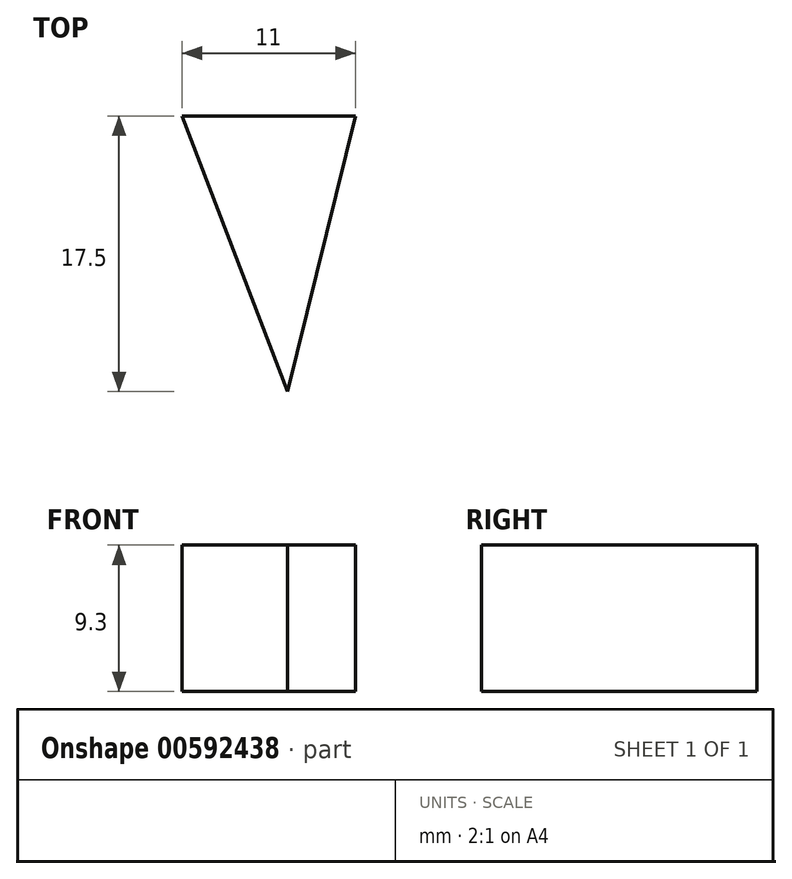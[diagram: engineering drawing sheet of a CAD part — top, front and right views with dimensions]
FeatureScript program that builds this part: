
annotation { "Feature Type Name" : "Feature", "Feature Type Description" : "" }
export const myFeature = defineFeature(function(context is Context, id is Id, definition is map)
    precondition{}
    {
        {
            var Q0;
            Q0=qCreatedBy(makeId("Top.planeOp"),FACE);
            var sketch = newSketch(context, id + "F0", { "sketchPlane" : qUnion([Q0])});
            skLineSegment(sketch, "E0", {"start": v(-29.08, -6.73) * mm, "end": v(-18.08, -6.73) * mm});
            skLineSegment(sketch, "E1", {"start": v(-22.38, -24.23) * mm, "end": v(-18.08, -6.73) * mm});
            skLineSegment(sketch, "E2", {"start": v(-29.08, -6.73) * mm, "end": v(-22.38, -24.23) * mm});
            skSolve(sketch);
        }
        {
            var Q0;
            Q0=makeQuery(id+"F0.imprint","IMPRINT",FACE,{"disambiguationData":[TD([[makeQuery(id+"F0.imprint","IMPRINT",EDGE,{"derivedFrom":sQuery(id+"F0.wireOp",EDGE,"E0")}),-1.0]])]});
            extrude(context, id + "F1", {"entities" : qUnion([Q0]), "depth" : 9.3 * mm, "offsetDistance" : 25 * mm});
        }
    });
